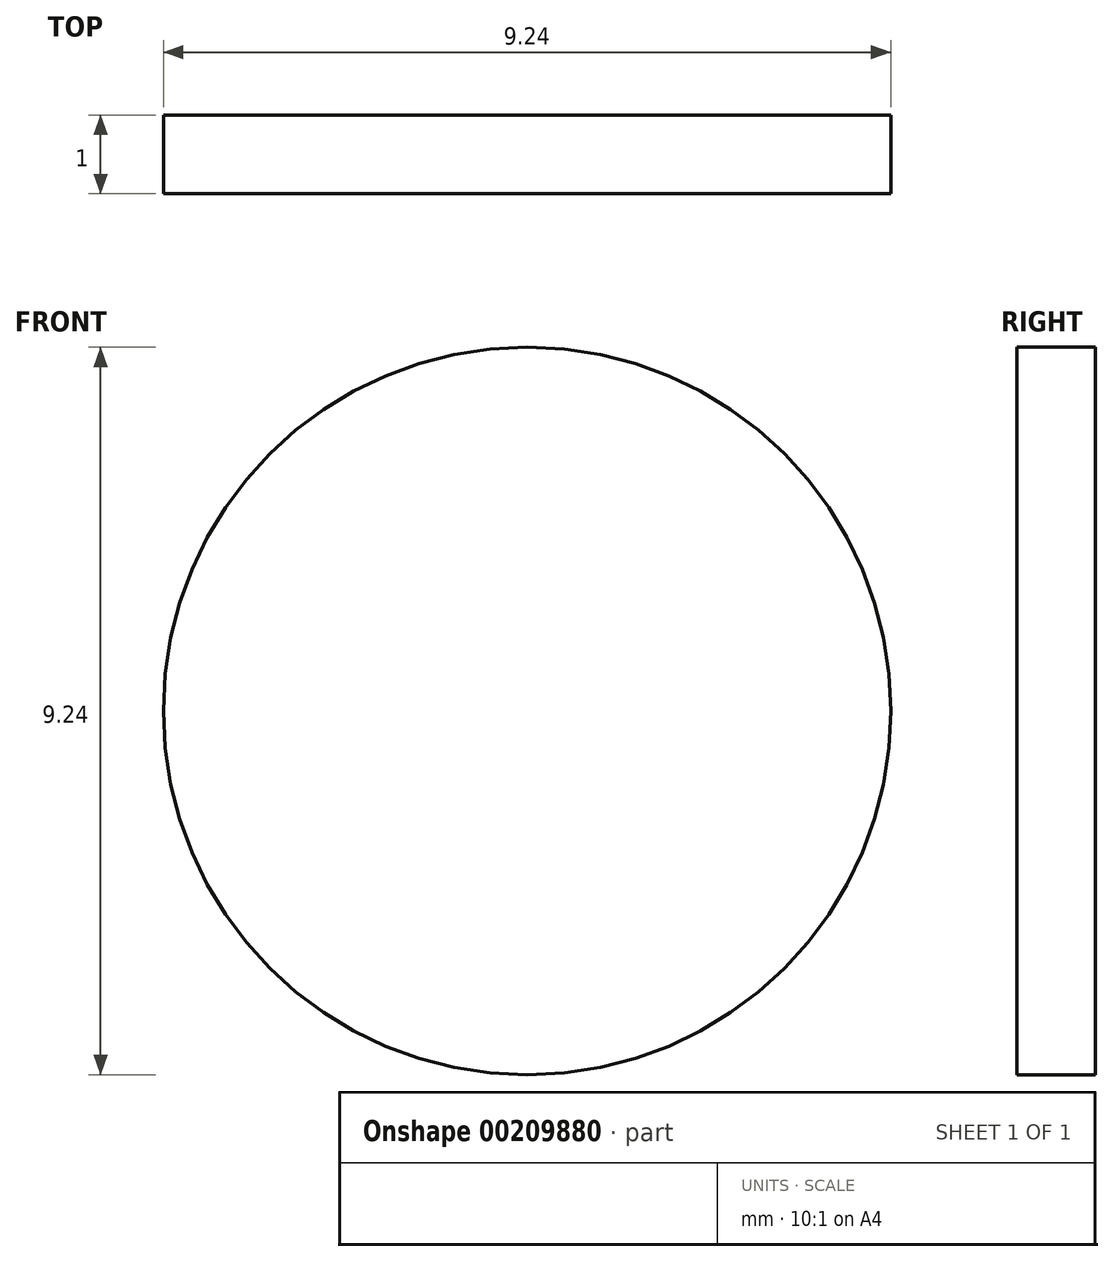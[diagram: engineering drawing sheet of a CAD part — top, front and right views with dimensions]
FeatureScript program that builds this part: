
annotation { "Feature Type Name" : "Feature", "Feature Type Description" : "" }
export const myFeature = defineFeature(function(context is Context, id is Id, definition is map)
    precondition{}
    {
        {
            var Q0;
            Q0=qCreatedBy(makeId("Front.planeOp"),FACE);
            var sketch = newSketch(context, id + "F0", { "sketchPlane" : qUnion([Q0])});
            skCircle(sketch, "E0", {"center": v(0, 0) * mm, "radius": 4.62 * mm});
            skSolve(sketch);
        }
        {
            var Q0;
            Q0=makeQuery(id+"F0.imprint","IMPRINT",FACE,{"disambiguationData":[TD([[makeQuery(id+"F0.imprint","IMPRINT",EDGE,{"derivedFrom":sQuery(id+"F0.wireOp",EDGE,"E0")}),1.0]])]});
            extrude(context, id + "F1", {"entities" : qUnion([Q0]), "depth" : 1 * mm});
        }
    });
